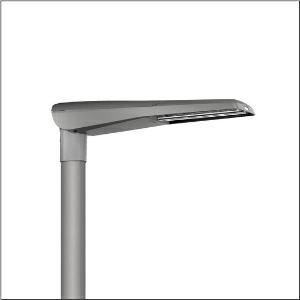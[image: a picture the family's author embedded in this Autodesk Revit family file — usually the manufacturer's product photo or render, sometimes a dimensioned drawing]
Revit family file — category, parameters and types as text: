
# Revit family: streetlight_sl_11_iq_mini___pc-r_5xc2fc1f08he_5d20
name_source: partatom
category: Lighting Fixtures
units: mm (PartAtom-declared; Revit-internal decimal feet)

## family parameters
Cut with Voids When Loaded = No
Host = Face
Light Source = No
Part Type = Normal
Room Calculation Point = No
Round Connector Dimension = Use Diameter
Shared = No

## types (1)
- --- (1 x LED, 5820 lm, 63.6 W, 2200K)
    Apparent Load = 64 VA
    CIE Flux Codes = 37 73 96 100 100
    Color Rendering = 70
    Color Temperature = 2200K
    Default Elevation = 1800 mm
    Description = Streetlight SL 11 iQ mini, mast luminaire, primary light control with 3 zone facetted reflector, of plastic, silver coated, highly specular, primary optical cover: cover, of PMMA, transparent, light distribution: PC-R, light emission: direct distribution, primary light characteristic: asymmetric, right, installation type: post-top, side-entry, lamps: LED, High Power LED, rated values: 7.110lm | 62,2W | 114,3lm/W (begin service life); end service life: 7.110lm | 65,6W; at 50% lumin. flux: 3.555lm | 29,4W | 120,9lm/W, colour temperature: 2200/2700/3000/4000K, colour rendering: CRI > 70, light colour: 722/727/730/740, light setting 1 begin service life: 100% | 7.110lm | 62,2W | 114,3lm/W | 3.000K, light setting 1 end service life: 65,6W, further light settings possible, control: Street-Remote, Auto-Match, Temp-Guard, Lumen-Switch, Night-Set, Smart-Wire, Light-Fading, Desk-Remote (wireless, voltage-free reading and setting of iQ features in the workshop via application-optimized NFC function/RFID function), optimised constant luminous flux control (CLO 2.0), with cable H07RN-F 5x 1.5mm², mains connection: 230..240V, AC, 50/60Hz, connection cable pre-assembled, cable length: 8,5m, luminaire housing, of diecast aluminium, powder-coated, Siteco® metallic grey (DB 702S), please order mast flange separately, inclination adjustable without tools: 0°, 5°, 10°, 15° (post-top) | 0°, -5°, -10°, -15° (side-entry), sealing non-destructively replaceable, multi-level sealing system, length: 736mm, width: 174mm, height: 116mm, mast flange for spigot size: 42mm (side-entry): 5XC10008XM4, 60/48mm (side-entry/post-top): 5XC10108XM2, 76/60mm (side-entry/post-top): 5XC10108XM1, equipment: Power, protection rating (complete): IP66, insulation class (complete): insulation class II (safety insulation), certification: CE, ENEC, ENEC+, VDE, impact resistance: IK10, permissible operating ambient temperature for outdoor applications: -25..+50°C, standard-compliant lighting for roads and squares, Environmental Product Declaration (EPD) tested and certified by an independent institute, packaging unit: 1 piece

Light Distribution: PC-R
    Height = 116 mm
    Lamp = 1 x LED
    Lamp Light Flux = 5820 lm
    Lamp Power = 63.6 W
    Lamp count = 1
    Length = 736 mm
    Luminous efficacy = 92 lm/W
    Manufacturer = Siteco
    ModVariant = No
    Model = 5XC2FC1F08HE
    Number of Poles = 1
    OnlyDefault = Yes
    Power Factor = 1
    Product Name = Streetlight SL 11 iQ mini | PC-R
    Product group = mast luminaire | pylon top
    ProductGroupID = 6100
    Protection Class = Protection class II
    Protection Degree = IP 66
    RLX_Detail_Level = 1
    RLX_Emergency_Light_Flux = 0 lm
    RLX_Emergency_Type = 0
    RLX_Emergency_Type_DB = No
    RlxData = <blob elided: 57501 chars, md5=9f17770e>
    Socket = socket
    Standby Power = 0 W
    System Light Flux = 5820 lm
    System Power = 64 W
    Type Comments = individual setting: luminous flux: 100 % | dim-lin: 254 | 866 mA
    Type Image = l_1003508.jpg
    URL = http://relux.com
    VarID = @adj_041053
    Voltage = 0 V
    Weight = 0.00 kg
    Width = 174 mm

## geometry (parser evidence)
native form markers: Blend x4, Sweep x11
no freeform markers — native parametric forms only
